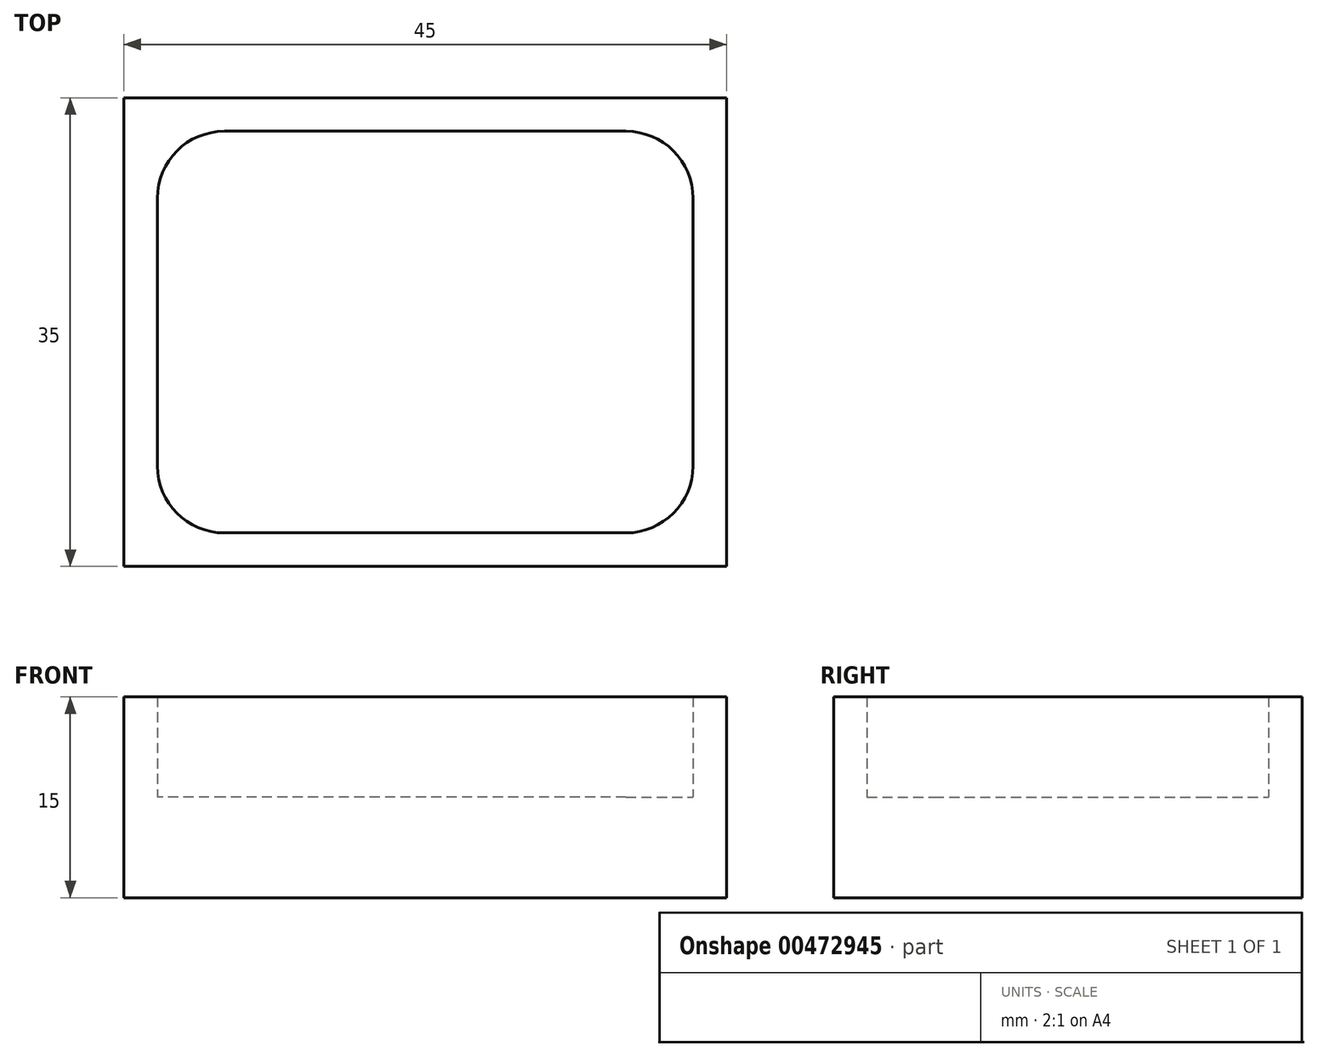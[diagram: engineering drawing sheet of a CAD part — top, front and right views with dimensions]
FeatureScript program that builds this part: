
annotation { "Feature Type Name" : "Feature", "Feature Type Description" : "" }
export const myFeature = defineFeature(function(context is Context, id is Id, definition is map)
    precondition{}
    {
        {
            var Q0;
            Q0=qCreatedBy(makeId("Top.planeOp"),FACE);
            var sketch = newSketch(context, id + "F0", { "sketchPlane" : qUnion([Q0])});
            skLineSegment(sketch, "E0.bottom", {"start": v(22.5, -17.5) * mm, "end": v(-22.5, -17.5) * mm});
            skLineSegment(sketch, "E0.top", {"start": v(22.5, 17.5) * mm, "end": v(-22.5, 17.5) * mm});
            skLineSegment(sketch, "E0.left", {"start": v(22.5, -17.5) * mm, "end": v(22.5, 17.5) * mm});
            skLineSegment(sketch, "E0.right", {"start": v(-22.5, -17.5) * mm, "end": v(-22.5, 17.5) * mm});
            skPoint(sketch, "E0.middle", {"position": v(0, 0) * mm});
            skSolve(sketch);
        }
        {
            var Q0;
            Q0 = qSketchRegion(id + "F0", true);
            extrude(context, id + "F1", {"entities" : qUnion([Q0]), "endBound" : BoundingType.SYMMETRIC, "depth" : 15 * mm});
        }
        {
            var Q0;
            Q0=qCreatedBy(makeId("Top.planeOp"),FACE);
            var sketch = newSketch(context, id + "F2", { "sketchPlane" : qUnion([Q0])});
            skLineSegment(sketch, "E1.bottom", {"start": v(20, -15) * mm, "end": v(-20, -15) * mm});
            skLineSegment(sketch, "E1.top", {"start": v(20, 15) * mm, "end": v(-20, 15) * mm});
            skLineSegment(sketch, "E1.left", {"start": v(20, -15) * mm, "end": v(20, 15) * mm});
            skLineSegment(sketch, "E1.right", {"start": v(-20, -15) * mm, "end": v(-20, 15) * mm});
            skPoint(sketch, "E1.middle", {"position": v(0, 0) * mm});
            skSolve(sketch);
        }
        {
            var Q0;
            Q0=makeQuery(id+"F2.imprint","IMPRINT",FACE,{"disambiguationData":[TD([[makeQuery(id+"F2.imprint","IMPRINT",EDGE,{"derivedFrom":sQuery(id+"F2.wireOp",EDGE,"E1.bottom")}),-1.0]])]});
            extrude(context, id + "F3", {"entities" : qUnion([Q0]), "operationType" : NewBodyOperationType.REMOVE, "depth" : 7.5 * mm});
        }
        {
            var Q0;
            Q0=qCreatedBy(makeId("Top.planeOp"),FACE);
            var sketch = newSketch(context, id + "F4", { "sketchPlane" : qUnion([Q0])});
            skLineSegment(sketch, "E2.bottom", {"start": v(20, -15) * mm, "end": v(-20, -15) * mm});
            skLineSegment(sketch, "E2.top", {"start": v(20, 15) * mm, "end": v(-20, 15) * mm});
            skLineSegment(sketch, "E2.left", {"start": v(20, -15) * mm, "end": v(20, 15) * mm});
            skLineSegment(sketch, "E2.right", {"start": v(-20, -15) * mm, "end": v(-20, 15) * mm});
            skPoint(sketch, "E2.middle", {"position": v(0, 0) * mm});
            skSolve(sketch);
        }
        {
            var Q0;
            Q0 = qSketchRegion(id + "F4", true);
            extrude(context, id + "F5", {"entities" : qUnion([Q0]), "operationType" : NewBodyOperationType.ADD, "oppositeDirection" : true, "depth" : 5 * mm});
        }
        {
            var Q0;
            Q0=makeQuery(id+"F3.boolean.opBoolean","COPY",EDGE,{"derivedFrom":makeQuery(id+"F3.opExtrude","SWEPT_EDGE",EDGE,{"disambiguationData":[OSD([sQuery(id+"F2.wireOp",EDGE,"E1.top"),sQuery(id+"F2.wireOp",EDGE,"E1.left")])]})});
            var Q1;
            Q1=makeQuery(id+"F3.boolean.opBoolean","COPY",EDGE,{"derivedFrom":makeQuery(id+"F3.opExtrude","SWEPT_EDGE",EDGE,{"disambiguationData":[OSD([sQuery(id+"F2.wireOp",EDGE,"E1.top"),sQuery(id+"F2.wireOp",EDGE,"E1.right")])]})});
            var Q2;
            Q2=makeQuery(id+"F3.boolean.opBoolean","COPY",EDGE,{"derivedFrom":makeQuery(id+"F3.opExtrude","SWEPT_EDGE",EDGE,{"disambiguationData":[OSD([sQuery(id+"F2.wireOp",EDGE,"E1.bottom"),sQuery(id+"F2.wireOp",EDGE,"E1.right")])]})});
            var Q3;
            Q3=makeQuery(id+"F3.boolean.opBoolean","COPY",EDGE,{"derivedFrom":makeQuery(id+"F3.opExtrude","SWEPT_EDGE",EDGE,{"disambiguationData":[OSD([sQuery(id+"F2.wireOp",EDGE,"E1.bottom"),sQuery(id+"F2.wireOp",EDGE,"E1.left")])]})});
            fillet(context, id + "F6", {"entities" : qUnion([Q0, Q1, Q2, Q3]), "radius" : 5 * mm, "tangentPropagation" : true, "allowEdgeOverflow" : false});
        }
    });
